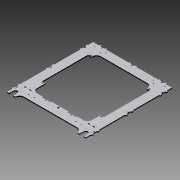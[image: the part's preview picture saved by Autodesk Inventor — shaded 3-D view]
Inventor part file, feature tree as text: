
AUTODESK INVENTOR PART (.ipt)
format: ipt  version: 2013 (Build 170138000, 138)  size: 667,136 bytes
history: native  units: mm
features: extrude x12, sketch x12, reference x6, mirror x5, fillet x3, pattern_linear x2
ambient origin geometry x8: Origin, YZ Plane, XZ Plane, XY Plane, X Axis, Y Axis, Z Axis, Center Point
bodies: Solid1 (feature_tree)
feature tree (40):
  extrude  "Extrusion1"  Depth=375.0mm
  extrude  "Extrusion2"  Depth=50.0mm
  extrude  "Extrusion3"  Depth=55.715mm
  mirror  "Mirror1"
  fillet  "Fillet1"  Radius=25.0mm
  fillet  "Fillet3"  Radius=50.0mm
  extrude  "Extrusion4"  Depth=5.715mm TaperAngle=0.0deg
  extrude  "Extrusion5"  Depth=10.0mm
  pattern_linear  "Rectangular Pattern1"  Count1=2  [1 undecoded]
  extrude  "Extrusion6"  Depth=4.0mm
  extrude  "Extrusion7"  Depth=25.0mm
  pattern_linear  "Rectangular Pattern2"  Spacing1=2.0mm  [1 undecoded]
  mirror  "Mirror2"
  extrude  "Extrusion8"  Depth=5.5mm
  mirror  "Mirror3"
  extrude  "Extrusion9"  Depth=3.0mm
  extrude  "Extrusion10"  Depth=8.285mm
  mirror  "Mirror4"
  fillet  "Fillet4"  Radius=6.285mm
  extrude  "Extrusion11"  Depth=5.715mm TaperAngle=0.0deg
  mirror  "Mirror5"
  extrude  "Extrusion12"  Depth=5.715mm
  sketch  "Sketch1"  dims[d0=323.0mm d2=375.0mm]
  sketch  "Sketch2"  dims[d3=75.0mm d4=70.0mm d5=50.0mm]
  sketch  "Sketch3"  dims[d6=70.0mm d7=55.715mm d8=25.0mm d9=50.0mm]
  sketch  "Sketch5"  dims[d10=50.0mm d11=5.715mm d12=0.0mm]
  sketch  "Sketch6"  dims[d13=290.0mm d15=10.0mm d16=20.0mm]
  sketch  "Sketch7"  dims[d17=75.0mm d18=4.0mm]
  sketch  "Sketch8"  dims[d19=5.715mm d20=0.0mm d21=25.0mm]
  sketch  "Sketch9"  dims[d22=8.0mm]
  sketch  "Sketch10"  dims[d24=1.5mm]
  reference  "Reference1"
  reference  "Reference2"
  reference  "Reference3"
  reference  "Reference4"
  reference  "Reference5"
  reference  "Reference6"
  sketch  "Sketch11"  dims[d25=4.0mm]
  sketch  "Sketch12"  dims[d26=5.715mm d27=0.0mm]
  sketch  "Sketch13"  dims[d29=2.0mm d30=2.0mm d32=5.5mm d33=3.0mm d34=8.285mm d35=6.285mm d36=5.715mm d37=0.0mm d38=5.715mm d40=10.0mm d41=25.0mm d42=5.715mm d43=0.0mm d44=30.0mm d46=175.0mm d47=5.715mm d48=0.0mm d49=5.715mm d50=0.0mm d51=30.0mm d53=200.0mm d54=25.0mm d55=25.0mm d56=31.0mm d57=3.0mm d58=23.0mm d59=10.0mm d60=0.0mm d61=3.0mm d63=10.0mm d64=0.0mm d65=12.0mm d66=14.0mm d67=3.0mm d68=2.0mm d69=5.5mm d70=10.0mm d71=0.0mm d72=2.0mm d73=138.0mm d74=16.0mm d75=16.0mm d76=25.0mm d77=17.0mm d78=16.0mm d79=25.0mm d80=5.0mm d81=10.0mm d82=0.0mm d83=8.0mm d84=10.0mm d85=10.0mm d86=0.0mm]
note: 2 required parameter values undecoded (feature->parameter linkage not recoverable at this tier; creation-order binding heuristic only, values carry confidence <= 0.55)
